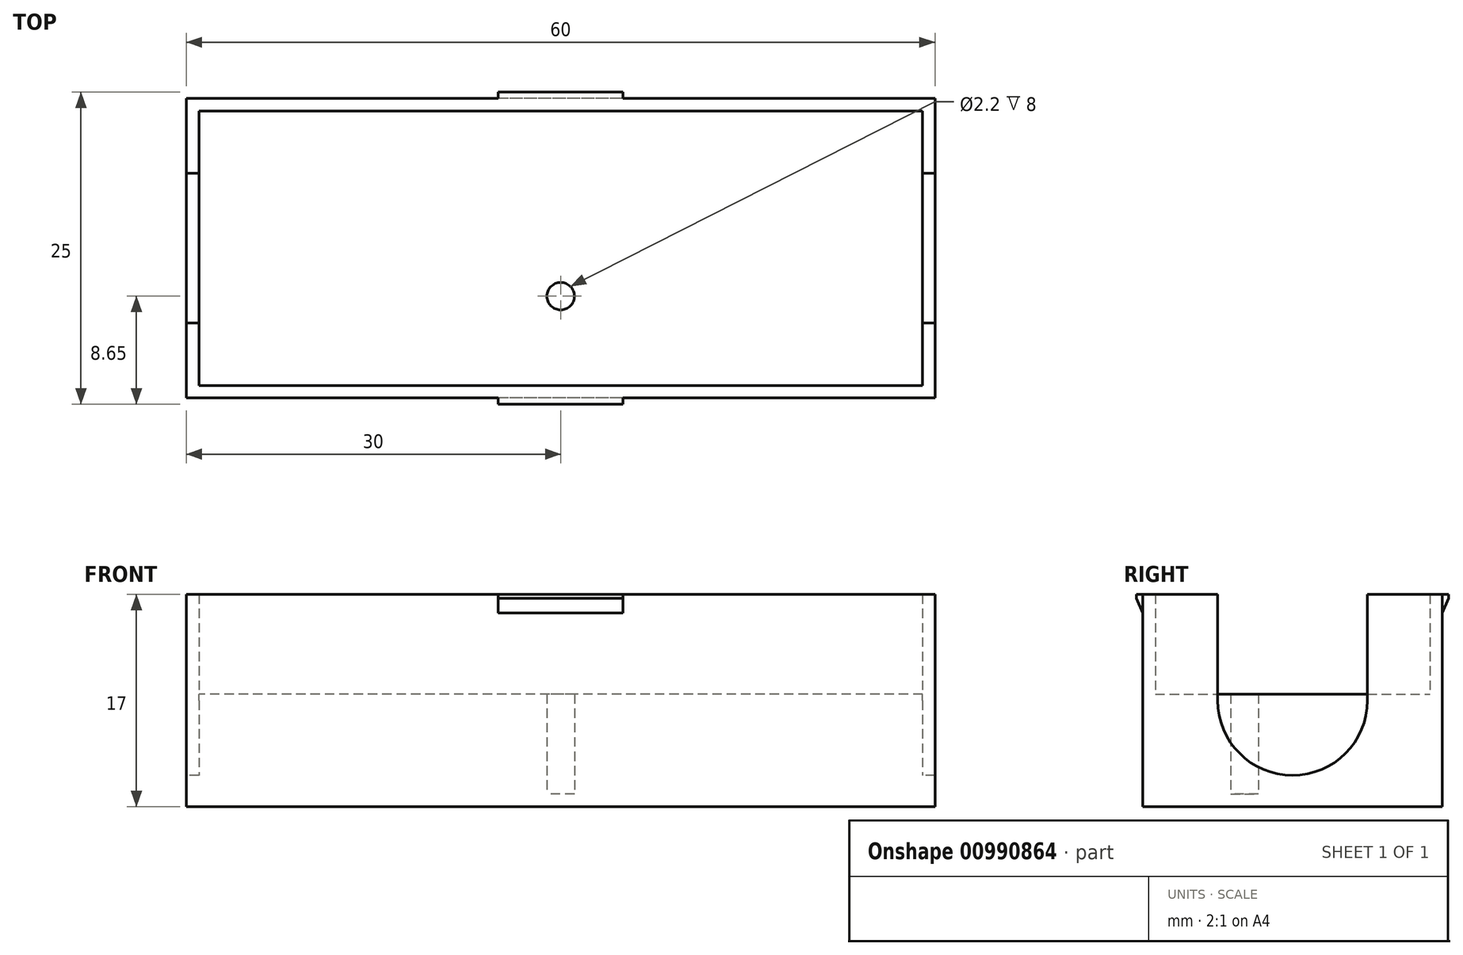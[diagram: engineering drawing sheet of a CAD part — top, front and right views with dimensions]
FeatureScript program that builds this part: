
annotation { "Feature Type Name" : "Feature", "Feature Type Description" : "" }
export const myFeature = defineFeature(function(context is Context, id is Id, definition is map)
    precondition{}
    {
        {
            var Q0;
            Q0=qCreatedBy(makeId("Top.planeOp"),FACE);
            var sketch = newSketch(context, id + "F0", { "sketchPlane" : qUnion([Q0])});
            skLineSegment(sketch, "E0.bottom", {"start": v(30, -12) * mm, "end": v(-30, -12) * mm});
            skLineSegment(sketch, "E0.top", {"start": v(30, 12) * mm, "end": v(-30, 12) * mm});
            skLineSegment(sketch, "E0.left", {"start": v(30, -12) * mm, "end": v(30, 12) * mm});
            skLineSegment(sketch, "E0.right", {"start": v(-30, -12) * mm, "end": v(-30, 12) * mm});
            skPoint(sketch, "E0.middle", {"position": v(0, 0) * mm});
            skSolve(sketch);
        }
        {
            var Q0;
            Q0 = qSketchRegion(id + "F0", true);
            extrude(context, id + "F1", {"entities" : qUnion([Q0]), "depth" : 17 * mm, "offsetDistance" : 25 * mm});
        }
        {
            var Q0;
            Q0=makeQuery(id+"F1.opExtrude","CAP_FACE",FACE,{"disambiguationData":[OSD([sQuery(id+"F0.wireOp",EDGE,"E0.bottom"),sQuery(id+"F0.wireOp",EDGE,"E0.top"),sQuery(id+"F0.wireOp",EDGE,"E0.left"),sQuery(id+"F0.wireOp",EDGE,"E0.right")])],"isStart":false});
            shell(context, id + "F2", {"entities" : qUnion([Q0]), "thickness" : 1 * mm});
        }
        {
            var Q0;
            Q0=makeQuery(id+"F1.opExtrude","SWEPT_FACE",FACE,{"disambiguationData":[OSD([sQuery(id+"F0.wireOp",EDGE,"E0.bottom")])]});
            var sketch = newSketch(context, id + "F3", { "sketchPlane" : qUnion([Q0])});
            skLineSegment(sketch, "E1.bottom", {"start": v(5, 15.5) * mm, "end": v(-5, 15.5) * mm});
            skLineSegment(sketch, "E1.left", {"start": v(5, 15.5) * mm, "end": v(5, 17) * mm});
            skLineSegment(sketch, "E1.right", {"start": v(-5, 15.5) * mm, "end": v(-5, 17) * mm});
            skPoint(sketch, "E1.middle", {"position": v(0, 17) * mm});
            skLineSegment(sketch, "E2", {"start": v(-5, 17) * mm, "end": v(5, 17) * mm});
            skPoint(sketch, "E3.orphan", {"position": v(-5, 18.5) * mm});
            skPoint(sketch, "E4.orphan", {"position": v(5, 18.5) * mm});
            skSolve(sketch);
        }
        {
            var Q0;
            Q0=makeQuery(id+"F3.imprint","IMPRINT",FACE,{"disambiguationData":[TD([[makeQuery(id+"F3.imprint","IMPRINT",EDGE,{"derivedFrom":sQuery(id+"F3.wireOp",EDGE,"E1.bottom")}),-1.0]])]});
            extrude(context, id + "F4", {"entities" : qUnion([Q0]), "operationType" : NewBodyOperationType.ADD, "depth" : .5 * mm, "offsetDistance" : 25 * mm});
        }
        {
            var Q0;
            Q0=makeQuery(id+"F4.opExtrude","CAP_EDGE",EDGE,{"disambiguationData":[OSD([sQuery(id+"F3.wireOp",EDGE,"E1.bottom")])],"isStart":false});
            chamfer(context, id + "F5", {"entities" : qUnion([Q0]), "chamferType" : ChamferType.TWO_OFFSETS, "width1" : .5 * mm, "oppositeDirection" : false, "width2" : 1.2 * mm, "tangentPropagation" : true});
        }
        {
            var Q0;
            Q0=makeQuery(id+"F1.opExtrude","SWEPT_BODY",BODY,{"disambiguationData":[OSD([sQuery(id+"F0.wireOp",EDGE,"E0.bottom"),sQuery(id+"F0.wireOp",EDGE,"E0.top"),sQuery(id+"F0.wireOp",EDGE,"E0.left"),sQuery(id+"F0.wireOp",EDGE,"E0.right")])]});
            var Q1;
            Q1=qCreatedBy(makeId("Front.planeOp"),FACE);
            mirror(context, id + "F6", {"operationType" : NewBodyOperationType.ADD, "entities" : qUnion([Q0]), "mirrorPlane" : qUnion([Q1])});
        }
        {
            var Q0;
            Q0=makeQuery(id+"F1.opExtrude","SWEPT_FACE",FACE,{"disambiguationData":[OSD([sQuery(id+"F0.wireOp",EDGE,"E0.right")])]});
            var sketch = newSketch(context, id + "F7", { "sketchPlane" : qUnion([Q0])});
            skLineSegment(sketch, "E5", {"start": v(-12, 17) * mm, "end": v(12, 0) * mm, "construction": true});
            skLineSegment(sketch, "E6", {"start": v(-12, 0) * mm, "end": v(12, 17) * mm, "construction": true});
            skArc(sketch, "E7", {"start": v(-6, 8.5) * mm, "mid": v(0, 2.5) * mm, "end": v(6, 8.5) * mm});
            skLineSegment(sketch, "E8", {"start": v(-12, 8.5) * mm, "end": v(12, 8.5) * mm, "construction": true});
            skLineSegment(sketch, "E9", {"start": v(-6, 8.5) * mm, "end": v(-6, 17) * mm});
            skLineSegment(sketch, "E10", {"start": v(6, 8.5) * mm, "end": v(6, 17) * mm});
            skSolve(sketch);
        }
        {
            var Q0;
            Q0 = qSketchRegion(id + "F7", true);
            var Q1;
            Q1=makeQuery(id+"F7.imprint","IMPRINT",FACE,{"disambiguationData":[TD([[makeQuery(id+"F7.imprint","IMPRINT",EDGE,{"derivedFrom":sQuery(id+"F7.wireOp",EDGE,"E7")}),1.0]])]});
            extrude(context, id + "F8", {"entities" : qUnion([Q0, Q1]), "operationType" : NewBodyOperationType.REMOVE, "endBound" : BoundingType.THROUGH_ALL, "oppositeDirection" : true, "depth" : 25 * mm, "offsetDistance" : 25 * mm});
        }
        {
            var Q0;
            Q0=makeQuery(id+"F2.opShell","OFFSET_FACE",FACE,{"disambiguationData":[OSD([sQuery(id+"F0.wireOp",EDGE,"E0.bottom"),sQuery(id+"F0.wireOp",EDGE,"E0.top"),sQuery(id+"F0.wireOp",EDGE,"E0.left"),sQuery(id+"F0.wireOp",EDGE,"E0.right")])]});
            var sketch = newSketch(context, id + "F9", { "sketchPlane" : qUnion([Q0])});
            skLineSegment(sketch, "E11", {"start": v(0, 11) * mm, "end": v(0, -11) * mm, "construction": true});
            skCircle(sketch, "E12", {"center": v(0, 3.85) * mm, "radius": 1.1 * mm});
            skLineSegment(sketch, "E13", {"start": v(-29, 0) * mm, "end": v(29, 0) * mm, "construction": true});
            skCircle(sketch, "E14.MirrorC", {"center": v(0, -3.85) * mm, "radius": 1.1 * mm});
            skSolve(sketch);
        }
        {
            var Q0;
            Q0=makeQuery(id+"F9.imprint","IMPRINT",FACE,{"disambiguationData":[TD([[makeQuery(id+"F9.imprint","IMPRINT",EDGE,{"derivedFrom":sQuery(id+"F9.wireOp",EDGE,"E12")}),1.0]])]});
            var Q1;
            Q1=makeQuery(id+"F9.imprint","IMPRINT",FACE,{"disambiguationData":[TD([[makeQuery(id+"F9.imprint","IMPRINT",EDGE,{"derivedFrom":sQuery(id+"F9.wireOp",EDGE,"E14.MirrorC")}),-1.0]])]});
            extrude(context, id + "F10", {"entities" : qUnion([Q0, Q1]), "operationType" : NewBodyOperationType.ADD, "depth" : 8 * mm, "offsetDistance" : 25 * mm});
        }
    });
